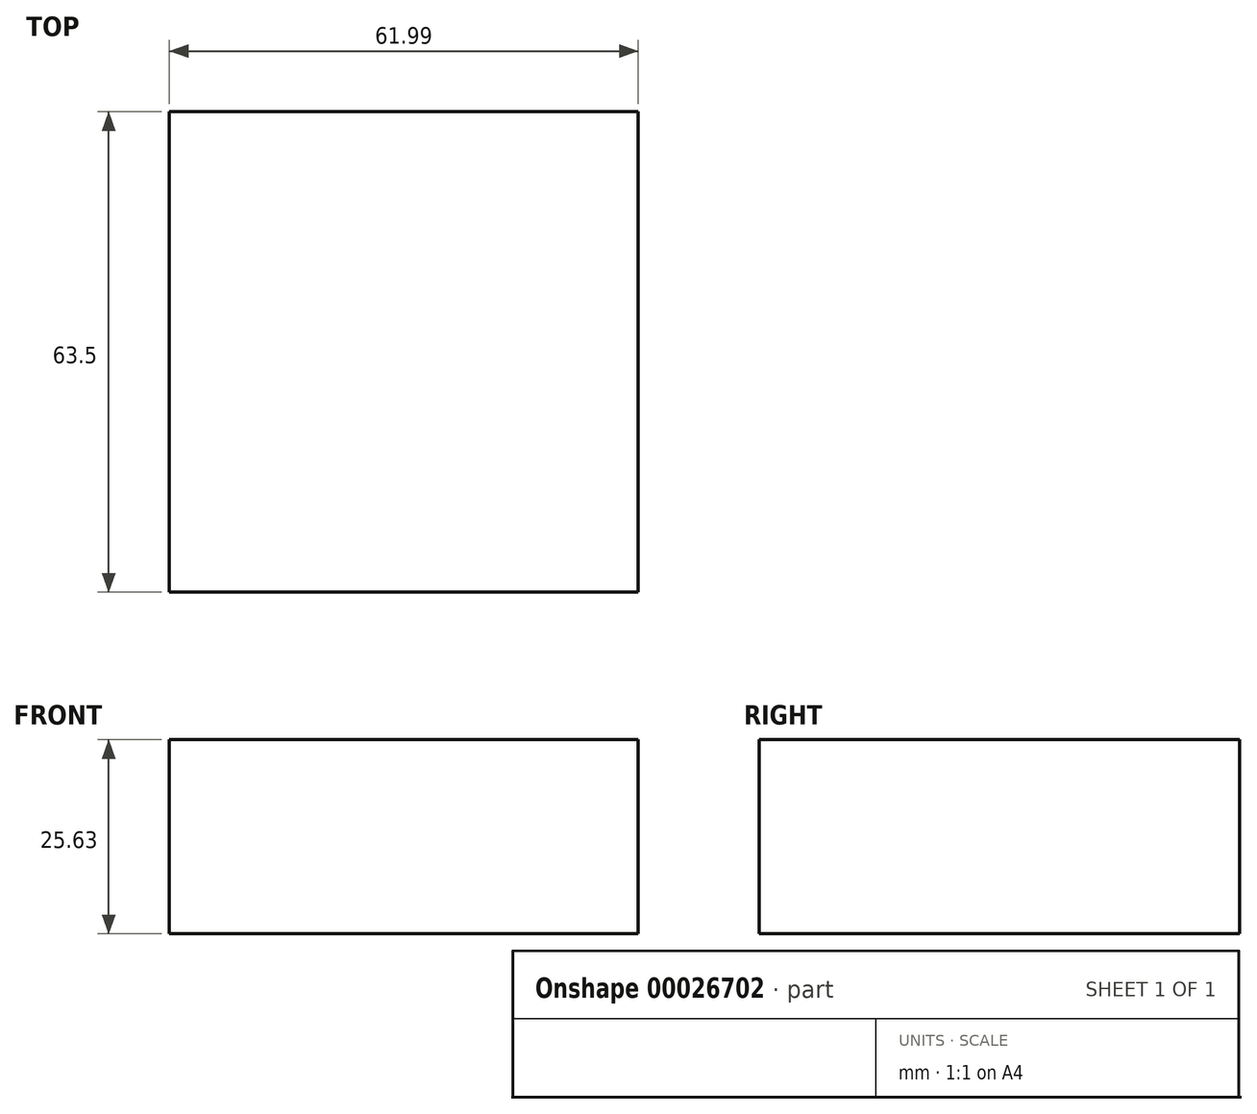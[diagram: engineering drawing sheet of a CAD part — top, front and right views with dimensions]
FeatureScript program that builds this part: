
annotation { "Feature Type Name" : "Feature", "Feature Type Description" : "" }
export const myFeature = defineFeature(function(context is Context, id is Id, definition is map)
    precondition{}
    {
        {
            var Q0;
            Q0=qCreatedBy(makeId("Front.planeOp"),FACE);
            var sketch = newSketch(context, id + "F0", { "sketchPlane" : qUnion([Q0])});
            skLineSegment(sketch, "E0.rect.bottom", {"start": v(-49.47, 34.42) * mm, "end": v(12.52, 34.42) * mm});
            skLineSegment(sketch, "E0.rect.top", {"start": v(-49.47, 8.8) * mm, "end": v(12.52, 8.8) * mm});
            skLineSegment(sketch, "E0.rect.left", {"start": v(-49.47, 34.42) * mm, "end": v(-49.47, 8.8) * mm});
            skLineSegment(sketch, "E0.rect.right", {"start": v(12.52, 34.42) * mm, "end": v(12.52, 8.8) * mm});
            skPoint(sketch, "E0.rect.middle", {"position": v(-18.48, 21.6) * mm});
            skSolve(sketch);
        }
        {
            var Q0;
            Q0 = qSketchRegion(id + "F0", true);
            extrude(context, id + "F1", {"entities" : qUnion([Q0]), "depth" : 63.5 * mm});
        }
    });
